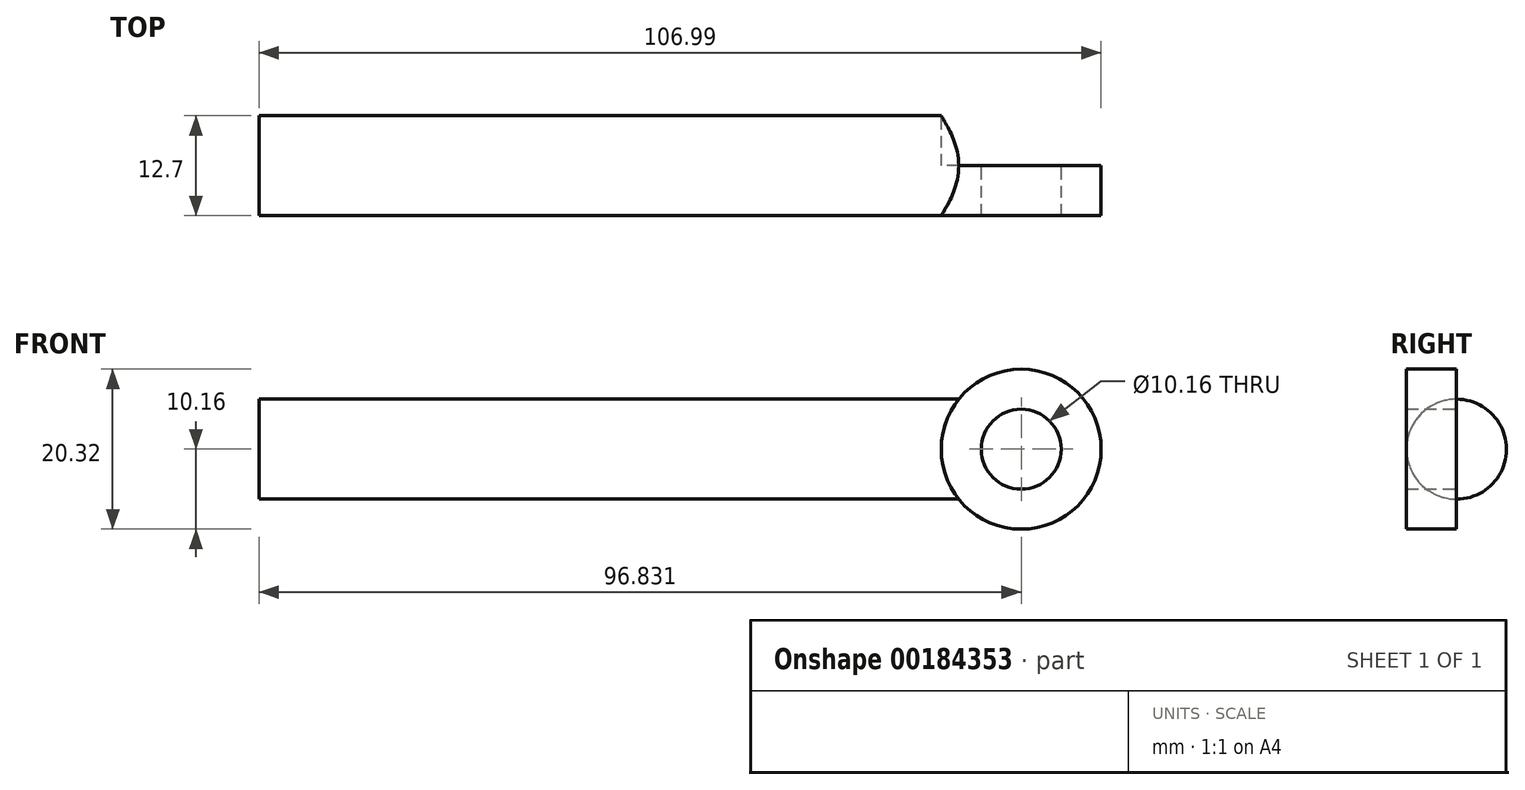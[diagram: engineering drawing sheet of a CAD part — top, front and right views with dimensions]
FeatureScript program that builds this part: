
annotation { "Feature Type Name" : "Feature", "Feature Type Description" : "" }
export const myFeature = defineFeature(function(context is Context, id is Id, definition is map)
    precondition{}
    {
        {
            var Q0;
            Q0=qCreatedBy(makeId("Front.planeOp"),FACE);
            var sketch = newSketch(context, id + "F0", { "sketchPlane" : qUnion([Q0])});
            skLineSegment(sketch, "E0.bottom", {"start": v(-44.45, 6.35) * mm, "end": v(44.45, 6.35) * mm});
            skLineSegment(sketch, "E0.top", {"start": v(-44.45, -6.35) * mm, "end": v(44.45, -6.35) * mm});
            skLineSegment(sketch, "E0.left", {"start": v(-44.45, 6.35) * mm, "end": v(-44.45, -6.35) * mm});
            skLineSegment(sketch, "E0.right", {"start": v(44.45, 6.35) * mm, "end": v(44.45, -6.35) * mm});
            skPoint(sketch, "E0.middle", {"position": v(0, 0) * mm});
            skCircle(sketch, "E1", {"center": v(52.38, 0) * mm, "radius": 10.16 * mm});
            skPoint(sketch, "E1.third.point", {"position": v(62.54, 0) * mm});
            skCircle(sketch, "E2", {"center": v(-52.38, 0) * mm, "radius": 10.16 * mm});
            skPoint(sketch, "E2.third.point", {"position": v(-62.54, 0) * mm});
            skPoint(sketch, "E2.third.point.positionSnap0", {"position": v(-44.45, 0) * mm});
            skCircle(sketch, "E3", {"center": v(52.38, 0) * mm, "radius": 5.08 * mm});
            skCircle(sketch, "E4", {"center": v(-52.38, 0) * mm, "radius": 4.83 * mm});
            skSolve(sketch);
        }
        {
            var Q0;
            {var subQ0=sQuery(id+"F0.wireOp",EDGE,"E0.bottom");Q0=makeQuery(id+"F0.imprint","IMPRINT",FACE,{"disambiguationData":[TD([[makeQuery(id+"F0.imprint","IMPRINT",EDGE,{"derivedFrom":subQ0}),-1.0]])]});}
            var Q1;
            {var subQ0=sQuery(id+"F0.wireOp",EDGE,"E0.left");Q1=makeQuery(id+"F0.imprint","IMPRINT",FACE,{"disambiguationData":[TD([[makeQuery(id+"F0.imprint","IMPRINT",EDGE,{"derivedFrom":subQ0}),1.0]])]});}
            extrude(context, id + "F1", {"entities" : qUnion([Q0, Q1]), "endBound" : BoundingType.SYMMETRIC, "depth" : 12.7 * mm});
        }
        {
            var Q0;
            Q0=makeQuery(id+"F1.opExtrude","CAP_EDGE",EDGE,{"disambiguationData":[OSD([sQuery(id+"F0.wireOp",EDGE,"E0.bottom")])],"isStart":false});
            var Q1;
            Q1=makeQuery(id+"F1.opExtrude","CAP_EDGE",EDGE,{"disambiguationData":[OSD([sQuery(id+"F0.wireOp",EDGE,"E0.bottom")])],"isStart":true});
            var Q2;
            Q2=makeQuery(id+"F1.opExtrude","CAP_EDGE",EDGE,{"disambiguationData":[OSD([sQuery(id+"F0.wireOp",EDGE,"E0.top")])],"isStart":false});
            var Q3;
            Q3=makeQuery(id+"F1.opExtrude","CAP_EDGE",EDGE,{"disambiguationData":[OSD([sQuery(id+"F0.wireOp",EDGE,"E0.top")])],"isStart":true});
            fillet(context, id + "F2", {"entities" : qUnion([Q0, Q1, Q2, Q3]), "radius" : 6.35 * mm, "tangentPropagation" : true, "allowEdgeOverflow" : false});
        }
        {
            var Q0;
            {var subQ0=sQuery(id+"F0.wireOp",EDGE,"E0.right");Q0=makeQuery(id+"F0.imprint","IMPRINT",FACE,{"disambiguationData":[TD([[makeQuery(id+"F0.imprint","IMPRINT",EDGE,{"derivedFrom":subQ0}),1.0]])]});}
            var Q1;
            {var subQ0=sQuery(id+"F0.wireOp",EDGE,"E0.right");Q1=makeQuery(id+"F0.imprint","IMPRINT",FACE,{"disambiguationData":[TD([[makeQuery(id+"F0.imprint","IMPRINT",EDGE,{"derivedFrom":subQ0}),-1.0]])]});}
            extrude(context, id + "F3", {"entities" : qUnion([Q0, Q1]), "operationType" : NewBodyOperationType.ADD, "depth" : 6.35 * mm});
        }
    });
